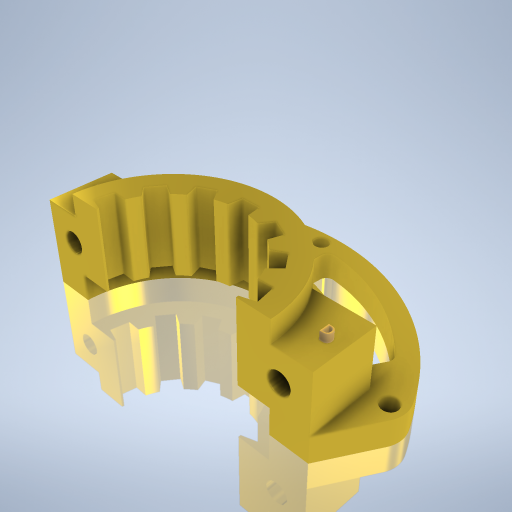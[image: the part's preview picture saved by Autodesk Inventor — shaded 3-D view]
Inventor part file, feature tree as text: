
AUTODESK INVENTOR PART (.ipt)
format: ipt  version: 2024.2 (Build 282272000, 272)  size: 476,160 bytes
history: native  units: mm
features: sketch x11, extrude x6, hole x4, mirror x3, projected_geometry x2, plane x1, pattern_circular x1, fillet x1, other x1
ambient origin geometry x8: Origin, YZ Plane, XZ Plane, XY Plane, X Axis, Y Axis, Z Axis, Center Point
bodies: Volumenkörper1 (feature_tree)
feature tree (30):
  extrude  "Extrusion1"  Depth=30.0mm TaperAngle=0.0deg
  extrude  "Extrusion2"  Depth=30.0mm TaperAngle=0.0deg
  extrude  "Extrusion3"  TaperAngle=120.0deg  [1 undecoded]
  extrude  "Extrusion4"  Depth=10.0mm TaperAngle=0.0deg
  plane  "Arbeitsebene1"
  pattern_circular  "Runde Anordnung1"  Count=4  [1 undecoded]
  mirror  "Spiegeln1"
  fillet  "Rundung1"  Radius=10.0mm
  extrude  "Extrusion5"  Depth=24.0mm
  hole  "Bohrung1"  [1 undecoded]
  hole  "Bohrung2"  [1 undecoded]
  extrude  "Extrusion6"  Depth=65.0mm
  mirror  "Spiegeln2"
  hole  "Bohrung3"  [1 undecoded]
  hole  "Bohrung5"  [1 undecoded]
  mirror  "Spiegeln3"
  other  "Prägen1"
  sketch  "Skizze1"  dims[d0=41.0mm d1=30.0mm d2=0.0mm]
  sketch  "Skizze2"  dims[d3=29.0mm d4=30.0mm d5=0.0mm]
  sketch  "Skizze3"  dims[d7=110.0mm d8=120.0deg]
  projected_geometry  "Projizierte Kontur1"
  sketch  "Skizze4"  dims[d9=72.0mm d10=10.0mm d11=0.0mm]
  projected_geometry  "Projizierte Kontur2"
  sketch  "Skizze5"  dims[d12=34.0mm]
  sketch  "Skizze6"  dims[d13=15.0deg]
  sketch  "Skizze7"  dims[d14=7.0mm]
  sketch  "Skizze9"  dims[d15=10.0mm d16=0.0mm d17=0.0mm d18=40.0mm d19=13.962634mm d21=10.0mm]
  sketch  "Skizze10"  dims[d22=24.0mm d23=24.0mm]
  sketch  "Skizze12"  dims[d24=22.0mm d25=0.0mm]
  sketch  "Skizze13"  dims[d26=8.0mm d27=6.0mm d28=4.0mm d29=2.0mm d30=90.0deg d31=8.0mm d32=0.0mm d33=8.0mm d34=6.0mm d35=4.0mm d36=2.0mm d37=90.0deg d38=8.0mm d39=0.0mm d50=1.570796mm d51=50.0mm d52=65.0mm d53=3.0mm d54=5.0mm d55=22.0mm d56=0.0mm d57=6.0mm d58=6.0mm d59=4.0mm d60=2.0mm d61=90.0deg d62=8.0mm d63=0.0mm d64=5.0mm d72=6.0mm d73=6.0mm d74=4.0mm d75=2.0mm d76=90.0deg d77=8.0mm d78=0.0mm d80=5.0mm d81=3.0mm d82=0.0mm]
note: 6 required parameter values undecoded (feature->parameter linkage not recoverable at this tier; creation-order binding heuristic only, values carry confidence <= 0.55)
